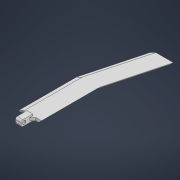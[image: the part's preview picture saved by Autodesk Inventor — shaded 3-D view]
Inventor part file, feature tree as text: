
AUTODESK INVENTOR PART (.ipt)
format: ipt  version: 2022 (Build 260153000, 153)  size: 182,784 bytes
history: native  units: in
note: dims shown in document units (in); Inventor stores cm internally (conversion verified against a paired STEP export)
features: sketch x8, extrude x4, fillet x2, plane x2, loft x2, chamfer x1
ambient origin geometry x8: Origin, YZ Plane, XZ Plane, XY Plane, X Axis, Y Axis, Z Axis, Center Point
bodies: Solid1 (feature_tree)
feature tree (19):
  extrude  "Extrusion1"  Depth=0.7874in
  extrude  "Extrusion2"  Depth=0.1969in
  fillet  "Fillet1"  [1 undecoded]
  fillet  "Fillet2"  Radius=0.0197in
  plane  "Work Plane1"
  plane  "Work Plane2"
  loft  "Loft4"
  sketch  "Sketch9"  dims[d31=0.1969in d32=0.5906in]
  extrude  "Extrusion3"  TaperAngle=0.0deg  [1 undecoded]
  extrude  "Extrusion4"  Depth=0.1969in
  chamfer  "Chamfer1"  Distance=0.3937in
  loft  "Loft5"
  sketch  "Sketch1"  dims[d0=0.3937in d1=0.7874in]
  sketch  "Sketch2"  dims[d2=0.3937in d3=0.0in d4=0.1969in d5=0.0in d6=0.0in d7=0.0197in]
  sketch  "Sketch7"  dims[d8=0.1181in d12=-0.0984in]
  sketch  "Sketch8"  dims[d13=-0.0984in d30=0.0in]
  sketch  "Sketch10"  dims[d33=3.937in]
  sketch  "Sketch11"  dims[d34=0.0in]
  sketch  "Sketch12"  dims[d35=0.5906in d36=0.3937in d37=3.937in d38=0.0in d39=90.0deg d40=0.0in d41=90.0deg d42=0.1969in d43=0.1969in d44=0.1969in d45=0.0in d46=0.1969in d47=0.0in d48=0.1969in d49=0.0492in d50=45.0deg d52=15.0deg d53=3.937in d54=3.937in d55=15.0deg d56=0.0in d57=90.0deg d58=0.0in d59=90.0deg]
note: 2 required parameter values undecoded (feature->parameter linkage not recoverable at this tier; creation-order binding heuristic only, values carry confidence <= 0.55)
